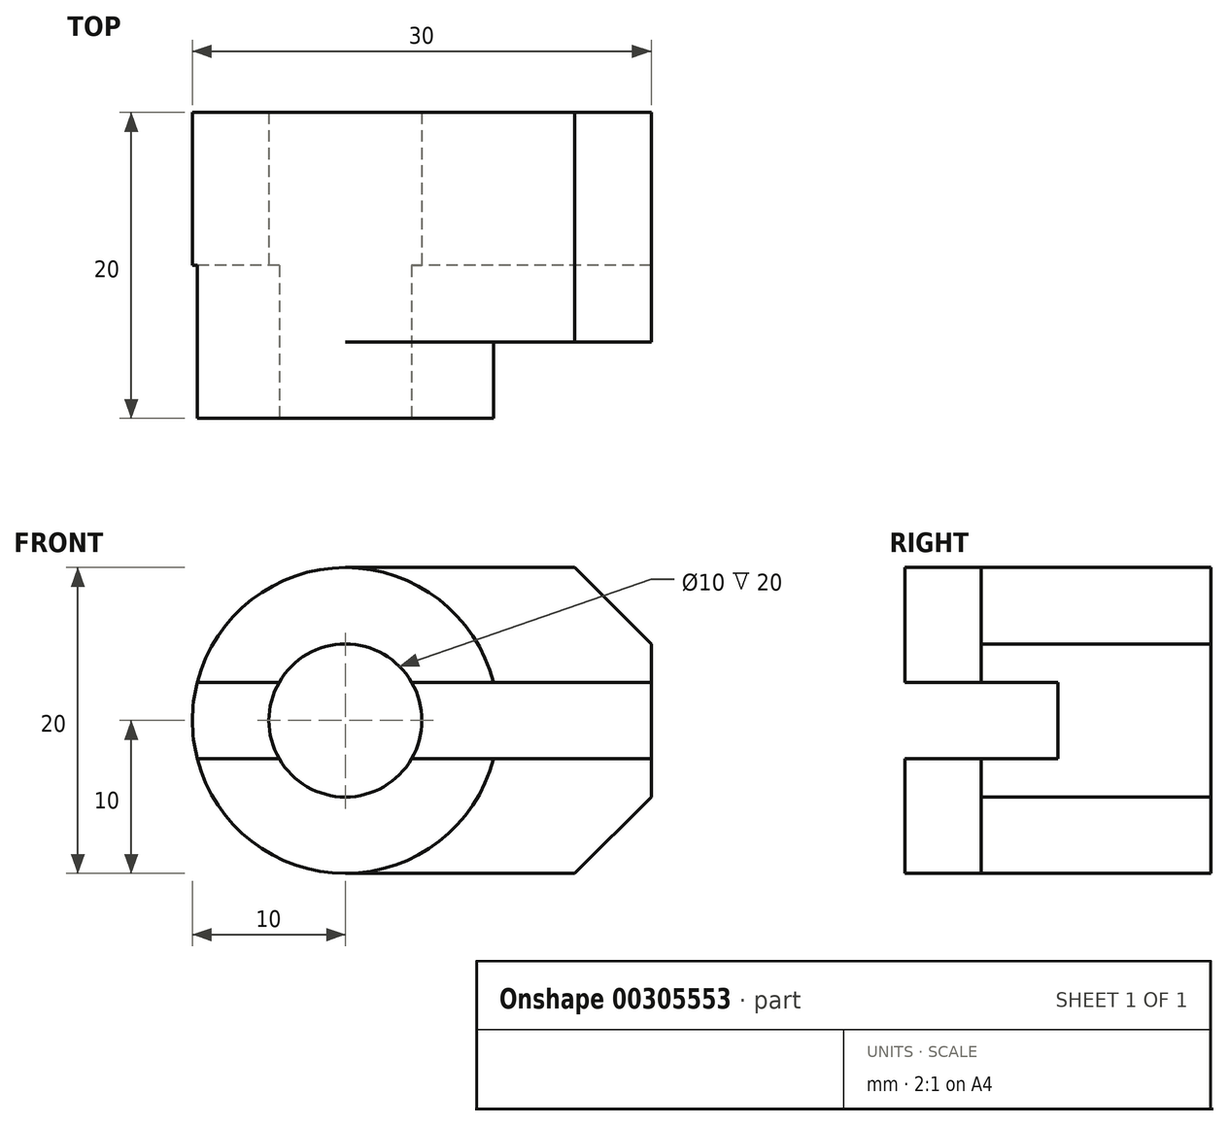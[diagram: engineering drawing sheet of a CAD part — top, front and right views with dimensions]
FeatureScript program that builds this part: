
annotation { "Feature Type Name" : "Feature", "Feature Type Description" : "" }
export const myFeature = defineFeature(function(context is Context, id is Id, definition is map)
    precondition{}
    {
        {
            var Q0;
            Q0=qCreatedBy(makeId("Top.planeOp"),FACE);
            var sketch = newSketch(context, id + "F0", { "sketchPlane" : qUnion([Q0])});
            skLineSegment(sketch, "E0.top", {"start": v(0, 20) * mm, "end": v(30, 20) * mm});
            skLineSegment(sketch, "E0.left", {"start": v(0, 0) * mm, "end": v(0, 20) * mm});
            skLineSegment(sketch, "E1", {"start": v(0, 0) * mm, "end": v(20, 0) * mm});
            skLineSegment(sketch, "E2", {"start": v(20, 0) * mm, "end": v(20, 5) * mm});
            skLineSegment(sketch, "E3", {"start": v(20, 5) * mm, "end": v(30, 5) * mm});
            skLineSegment(sketch, "E4", {"start": v(30, 5) * mm, "end": v(30, 20) * mm});
            skSolve(sketch);
        }
        {
            var Q0;
            Q0 = qSketchRegion(id + "F0", true);
            extrude(context, id + "F1", {"entities" : qUnion([Q0]), "depth" : 20 * mm});
        }
        {
            var Q0;
            Q0=makeQuery(id+"F1.opExtrude","CAP_EDGE",EDGE,{"disambiguationData":[OSD([sQuery(id+"F0.wireOp",EDGE,"E0.left")])],"isStart":false});
            var Q1;
            Q1=makeQuery(id+"F1.opExtrude","CAP_EDGE",EDGE,{"disambiguationData":[OSD([sQuery(id+"F0.wireOp",EDGE,"E0.left")])],"isStart":true});
            fillet(context, id + "F2", {"entities" : qUnion([Q0, Q1]), "radius" : 10 * mm, "tangentPropagation" : true, "allowEdgeOverflow" : false});
        }
        {
            var Q0;
            Q0=qCreatedBy(makeId("Front.planeOp"),FACE);
            var sketch = newSketch(context, id + "F3", { "sketchPlane" : qUnion([Q0])});
            skLineSegment(sketch, "E5", {"start": v(25, 20) * mm, "end": v(30, 15) * mm});
            skLineSegment(sketch, "E6", {"start": v(30, 15) * mm, "end": v(30, 20) * mm});
            skLineSegment(sketch, "E7", {"start": v(30, 20) * mm, "end": v(25, 20) * mm});
            skLineSegment(sketch, "E8", {"start": v(30, 5) * mm, "end": v(25, 0) * mm});
            skLineSegment(sketch, "E9", {"start": v(25, 0) * mm, "end": v(30, 0) * mm});
            skLineSegment(sketch, "E10", {"start": v(30, 0) * mm, "end": v(30, 5) * mm});
            skSolve(sketch);
        }
        {
            var Q0;
            Q0 = qSketchRegion(id + "F3", true);
            extrude(context, id + "F4", {"entities" : qUnion([Q0]), "operationType" : NewBodyOperationType.REMOVE, "oppositeDirection" : true, "depth" : 25 * mm});
        }
        {
            var Q0;
            Q0=makeQuery(id+"F1.opExtrude","SWEPT_FACE",FACE,{"disambiguationData":[OSD([sQuery(id+"F0.wireOp",EDGE,"E1")])]});
            var sketch = newSketch(context, id + "F5", { "sketchPlane" : qUnion([Q0])});
            skCircle(sketch, "E11", {"center": v(10, 10) * mm, "radius": 5 * mm});
            skSolve(sketch);
        }
        {
            var Q0;
            Q0 = qSketchRegion(id + "F5", true);
            extrude(context, id + "F6", {"entities" : qUnion([Q0]), "operationType" : NewBodyOperationType.REMOVE, "endBound" : BoundingType.THROUGH_ALL, "oppositeDirection" : true, "depth" : 25 * mm});
        }
        {
            var Q0;
            Q0=makeQuery(id+"F1.opExtrude","CAP_EDGE",EDGE,{"disambiguationData":[OSD([sQuery(id+"F0.wireOp",EDGE,"E2")])],"isStart":false});
            var Q1;
            Q1=makeQuery(id+"F1.opExtrude","CAP_EDGE",EDGE,{"disambiguationData":[OSD([sQuery(id+"F0.wireOp",EDGE,"E2")])],"isStart":true});
            fillet(context, id + "F7", {"entities" : qUnion([Q0, Q1]), "radius" : 10 * mm, "tangentPropagation" : true, "allowEdgeOverflow" : false});
        }
        {
            var Q0;
            Q0=qCreatedBy(makeId("Right.planeOp"),FACE);
            var sketch = newSketch(context, id + "F8", { "sketchPlane" : qUnion([Q0])});
            skLineSegment(sketch, "E12.bottom", {"start": v(0, 12.5) * mm, "end": v(10, 12.5) * mm});
            skLineSegment(sketch, "E12.top", {"start": v(0, 7.5) * mm, "end": v(10, 7.5) * mm});
            skLineSegment(sketch, "E12.left", {"start": v(0, 12.5) * mm, "end": v(0, 7.5) * mm});
            skLineSegment(sketch, "E12.right", {"start": v(10, 12.5) * mm, "end": v(10, 7.5) * mm});
            skSolve(sketch);
        }
        {
            var Q0;
            Q0 = qSketchRegion(id + "F8", true);
            extrude(context, id + "F9", {"entities" : qUnion([Q0]), "operationType" : NewBodyOperationType.REMOVE, "endBound" : BoundingType.THROUGH_ALL, "depth" : 25 * mm});
        }
    });
